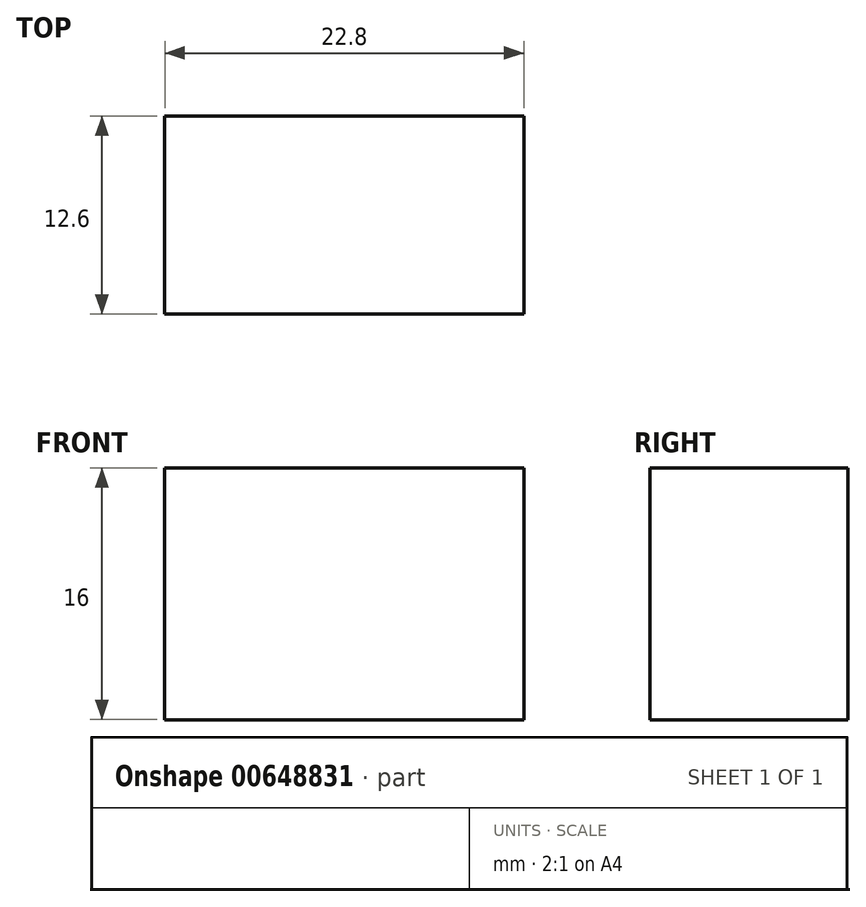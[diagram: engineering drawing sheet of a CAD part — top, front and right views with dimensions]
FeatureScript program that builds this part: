
annotation { "Feature Type Name" : "Feature", "Feature Type Description" : "" }
export const myFeature = defineFeature(function(context is Context, id is Id, definition is map)
    precondition{}
    {
        {
            var Q0;
            Q0=qCreatedBy(makeId("Front.planeOp"),FACE);
            var sketch = newSketch(context, id + "F0", { "sketchPlane" : qUnion([Q0])});
            skLineSegment(sketch, "E0", {"start": v(-33.8, -6.11) * mm, "end": v(-11, -6.11) * mm});
            skLineSegment(sketch, "E1", {"start": v(-11, -6.11) * mm, "end": v(-11, -22.11) * mm});
            skLineSegment(sketch, "E2", {"start": v(-11, -22.11) * mm, "end": v(-33.8, -22.11) * mm});
            skLineSegment(sketch, "E3", {"start": v(-33.8, -22.11) * mm, "end": v(-33.8, -6.11) * mm});
            skSolve(sketch);
        }
        {
            var Q0;
            Q0=makeQuery(id+"F0.imprint","IMPRINT",FACE,{"disambiguationData":[TD([[makeQuery(id+"F0.imprint","IMPRINT",EDGE,{"derivedFrom":sQuery(id+"F0.wireOp",EDGE,"E0")}),-1.0]])]});
            extrude(context, id + "F1", {"entities" : qUnion([Q0]), "oppositeDirection" : true, "depth" : 12.6 * mm, "offsetDistance" : 25 * mm});
        }
    });
